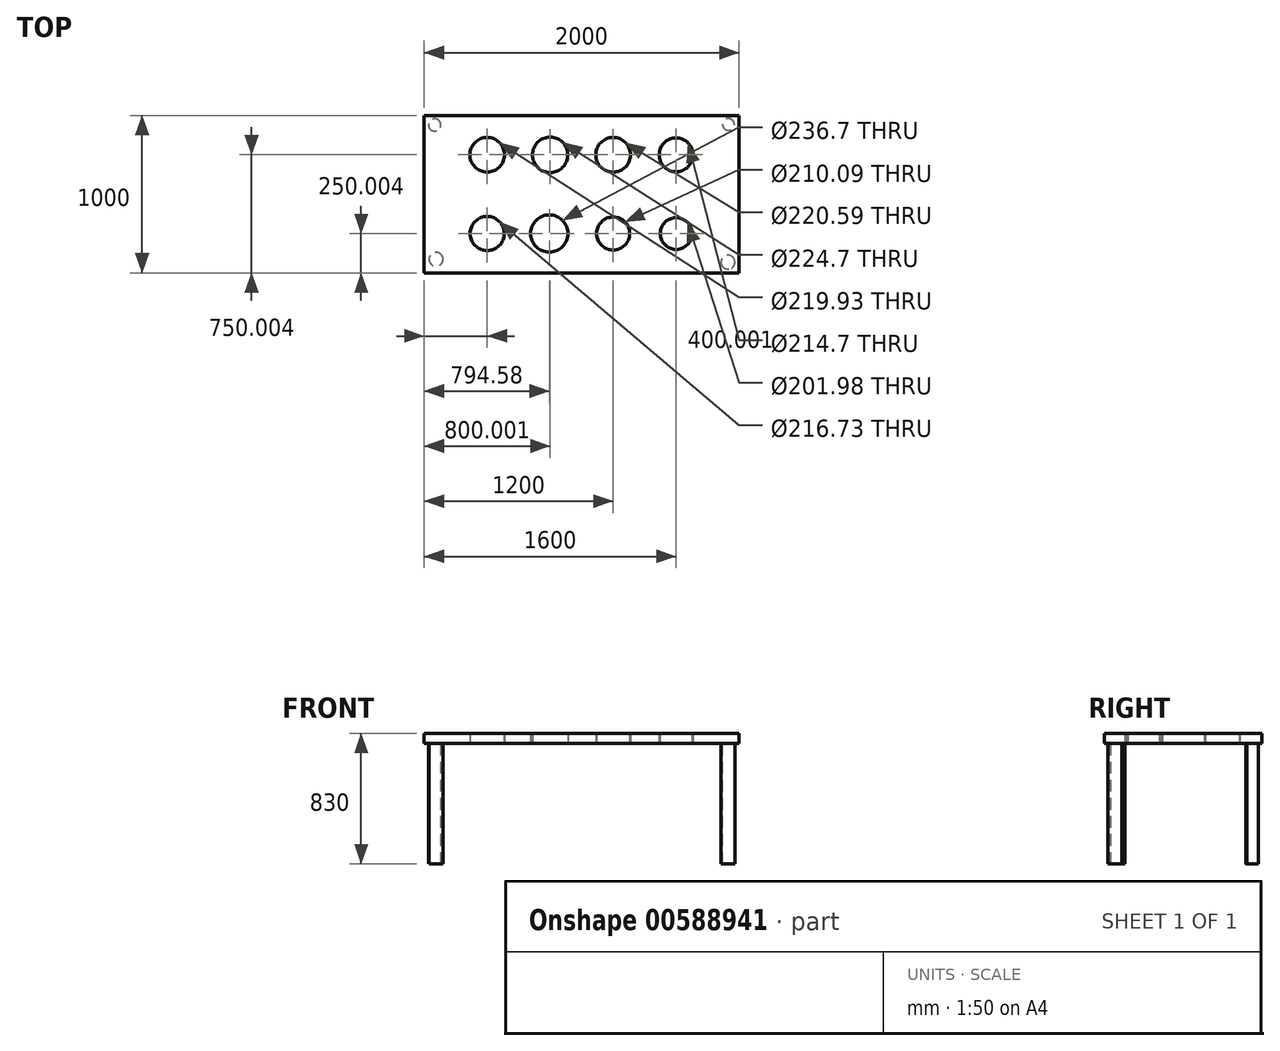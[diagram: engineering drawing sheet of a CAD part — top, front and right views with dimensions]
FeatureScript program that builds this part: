
annotation { "Feature Type Name" : "Feature", "Feature Type Description" : "" }
export const myFeature = defineFeature(function(context is Context, id is Id, definition is map)
    precondition{}
    {
        {
            var Q0;
            Q0=qCreatedBy(makeId("Top.planeOp"),FACE);
            var sketch = newSketch(context, id + "F0", { "sketchPlane" : qUnion([Q0])});
            skLineSegment(sketch, "E0.bottom", {"start": v(-794.58, 492.35) * mm, "end": v(1205.42, 492.35) * mm});
            skLineSegment(sketch, "E0.top", {"start": v(-794.58, -507.65) * mm, "end": v(1205.42, -507.65) * mm});
            skLineSegment(sketch, "E0.left", {"start": v(-794.58, 492.35) * mm, "end": v(-794.58, -507.65) * mm});
            skLineSegment(sketch, "E0.right", {"start": v(1205.42, 492.35) * mm, "end": v(1205.42, -507.65) * mm});
            skLineSegment(sketch, "E1", {"start": v(-794.58, 242.35) * mm, "end": v(1205.42, 242.35) * mm, "construction": true});
            skLineSegment(sketch, "E2", {"start": v(-794.58, -257.65) * mm, "end": v(1205.42, -257.65) * mm, "construction": true});
            skLineSegment(sketch, "E3", {"start": v(-394.58, 492.35) * mm, "end": v(-394.58, -507.65) * mm, "construction": true});
            skLineSegment(sketch, "E4", {"start": v(5.42, 492.35) * mm, "end": v(5.42, -507.65) * mm, "construction": true});
            skLineSegment(sketch, "E5", {"start": v(405.42, 492.35) * mm, "end": v(405.42, -507.65) * mm, "construction": true});
            skLineSegment(sketch, "E6", {"start": v(805.42, 492.35) * mm, "end": v(805.42, -507.65) * mm});
            skCircle(sketch, "E7", {"center": v(-394.58, 242.35) * mm, "radius": 109.96 * mm});
            skCircle(sketch, "E8", {"center": v(5.42, 242.35) * mm, "radius": 112.35 * mm});
            skCircle(sketch, "E9", {"center": v(405.42, 242.35) * mm, "radius": 110.3 * mm});
            skCircle(sketch, "E10", {"center": v(805.42, 242.35) * mm, "radius": 107.35 * mm});
            skCircle(sketch, "E11", {"center": v(805.42, -257.65) * mm, "radius": 101 * mm});
            skCircle(sketch, "E12", {"center": v(405.42, -257.65) * mm, "radius": 105.04 * mm});
            skCircle(sketch, "E13", {"center": v(0, -257.65) * mm, "radius": 118.35 * mm});
            skCircle(sketch, "E14", {"center": v(-394.58, -257.65) * mm, "radius": 108.36 * mm});
            skSolve(sketch);
        }
        {
            var Q0;
            {var subQ9=sQuery(id+"F0.wireOp",EDGE,"E0.left");Q0=makeQuery(id+"F0.imprint","IMPRINT",FACE,{"disambiguationData":[TD([[makeQuery(id+"F0.imprint","IMPRINT",EDGE,{"derivedFrom":subQ9}),1.0]])]});}
            var Q1;
            {var subQ0=sQuery(id+"F0.wireOp",EDGE,"E0.right");Q1=makeQuery(id+"F0.imprint","IMPRINT",FACE,{"disambiguationData":[TD([[makeQuery(id+"F0.imprint","IMPRINT",EDGE,{"derivedFrom":subQ0}),-1.0]])]});}
            extrude(context, id + "F1", {"entities" : qUnion([Q0, Q1]), "depth" : 64 * mm, "offsetDistance" : 25 * mm});
        }
        {
            var Q0;
            Q0=makeQuery(id+"F1.opExtrude","CAP_FACE",FACE,{"disambiguationData":[OSD([sQuery(id+"F0.wireOp",EDGE,"E0.bottom"),sQuery(id+"F0.wireOp",EDGE,"E0.top"),sQuery(id+"F0.wireOp",EDGE,"E0.left"),sQuery(id+"F0.wireOp",EDGE,"E0.right"),sQuery(id+"F0.wireOp",EDGE,"E7"),sQuery(id+"F0.wireOp",EDGE,"E8"),sQuery(id+"F0.wireOp",EDGE,"E9"),sQuery(id+"F0.wireOp",EDGE,"E10"),sQuery(id+"F0.wireOp",EDGE,"E11"),sQuery(id+"F0.wireOp",EDGE,"E12"),sQuery(id+"F0.wireOp",EDGE,"E13"),sQuery(id+"F0.wireOp",EDGE,"E14")])],"isStart":true});
            var sketch = newSketch(context, id + "F2", { "sketchPlane" : qUnion([Q0])});
            skLineSegment(sketch, "E15", {"start": v(-794.58, 507.65) * mm, "end": v(-718.9, 421.17) * mm});
            skLineSegment(sketch, "E16", {"start": v(-794.58, -492.35) * mm, "end": v(-728.1, -432.03) * mm});
            skLineSegment(sketch, "E17", {"start": v(1205.42, 507.65) * mm, "end": v(1134.83, 439.58) * mm});
            skLineSegment(sketch, "E18", {"start": v(1205.42, -492.35) * mm, "end": v(1137.9, -435.1) * mm});
            skCircle(sketch, "E19", {"center": v(-718.9, 421.17) * mm, "radius": 44.26 * mm});
            skCircle(sketch, "E20", {"center": v(-728.1, -432.03) * mm, "radius": 39.3 * mm});
            skCircle(sketch, "E21", {"center": v(1134.83, 439.58) * mm, "radius": 43.94 * mm});
            skCircle(sketch, "E22", {"center": v(1137.9, -435.1) * mm, "radius": 37.34 * mm});
            skSolve(sketch);
        }
        {
            var Q0;
            Q0=makeQuery(id+"F2.imprint","IMPRINT",FACE,{"disambiguationData":[TD([[makeQuery(id+"F2.imprint","IMPRINT",EDGE,{"derivedFrom":sQuery(id+"F2.wireOp",EDGE,"E21")}),1.0]])]});
            var Q1;
            Q1=makeQuery(id+"F2.imprint","IMPRINT",FACE,{"disambiguationData":[TD([[makeQuery(id+"F2.imprint","IMPRINT",EDGE,{"derivedFrom":sQuery(id+"F2.wireOp",EDGE,"E22")}),1.0]])]});
            var Q2;
            Q2=makeQuery(id+"F2.imprint","IMPRINT",FACE,{"disambiguationData":[TD([[makeQuery(id+"F2.imprint","IMPRINT",EDGE,{"derivedFrom":sQuery(id+"F2.wireOp",EDGE,"E19")}),1.0]])]});
            var Q3;
            Q3=makeQuery(id+"F2.imprint","IMPRINT",FACE,{"disambiguationData":[TD([[makeQuery(id+"F2.imprint","IMPRINT",EDGE,{"derivedFrom":sQuery(id+"F2.wireOp",EDGE,"E20")}),1.0]])]});
            extrude(context, id + "F3", {"entities" : qUnion([Q0, Q1, Q2, Q3]), "operationType" : NewBodyOperationType.ADD, "depth" : 766 * mm, "offsetDistance" : 25 * mm});
        }
    });
